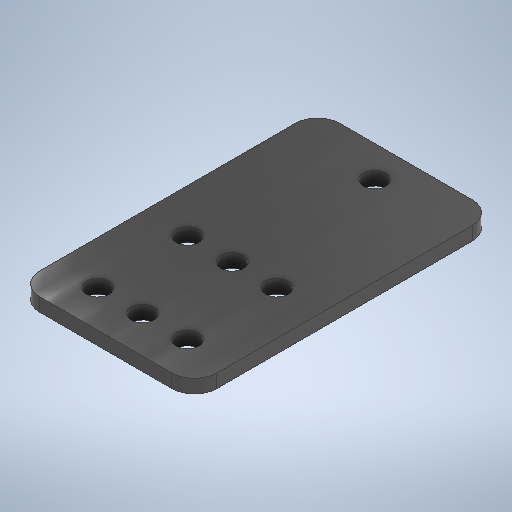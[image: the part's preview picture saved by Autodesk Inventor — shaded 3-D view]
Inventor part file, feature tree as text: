
AUTODESK INVENTOR PART (.ipt)
format: ipt  version: 2025.2 (Build 292293000, 293)  size: 261,632 bytes
history: native  units: in
note: dims shown in document units (in); Inventor stores cm internally (conversion verified against a paired STEP export)
features: plane x1
ambient origin geometry x8: Origin, YZ Plane, XZ Plane, XY Plane, X Axis, Y Axis, Z Axis, Center Point
bodies: Solid1 (feature_tree), Body1 (feature_tree)
feature tree (1):
  plane  "Work Plane1"
